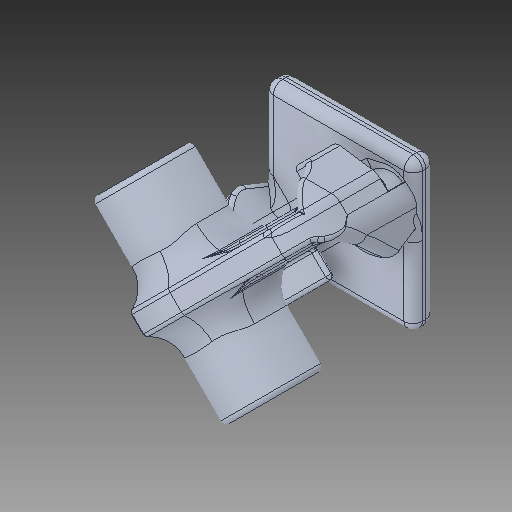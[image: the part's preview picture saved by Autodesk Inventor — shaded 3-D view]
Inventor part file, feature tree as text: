
AUTODESK INVENTOR PART (.ipt)
format: ipt  version: 2018 (Build 220112000, 112)  size: 1,180,160 bytes
history: native  units: in
note: dims shown in document units (in); Inventor stores cm internally (conversion verified against a paired STEP export)
features: fillet x1
ambient origin geometry x8: Origin, YZ Plane, XZ Plane, XY Plane, X Axis, Y Axis, Z Axis, Center Point
bodies: Solid1 (feature_tree)
feature tree (1):
  fillet  "Fillet119"  [1 undecoded]
note: 1 required parameter value undecoded (feature->parameter linkage not recoverable at this tier; creation-order binding heuristic only, values carry confidence <= 0.55)
